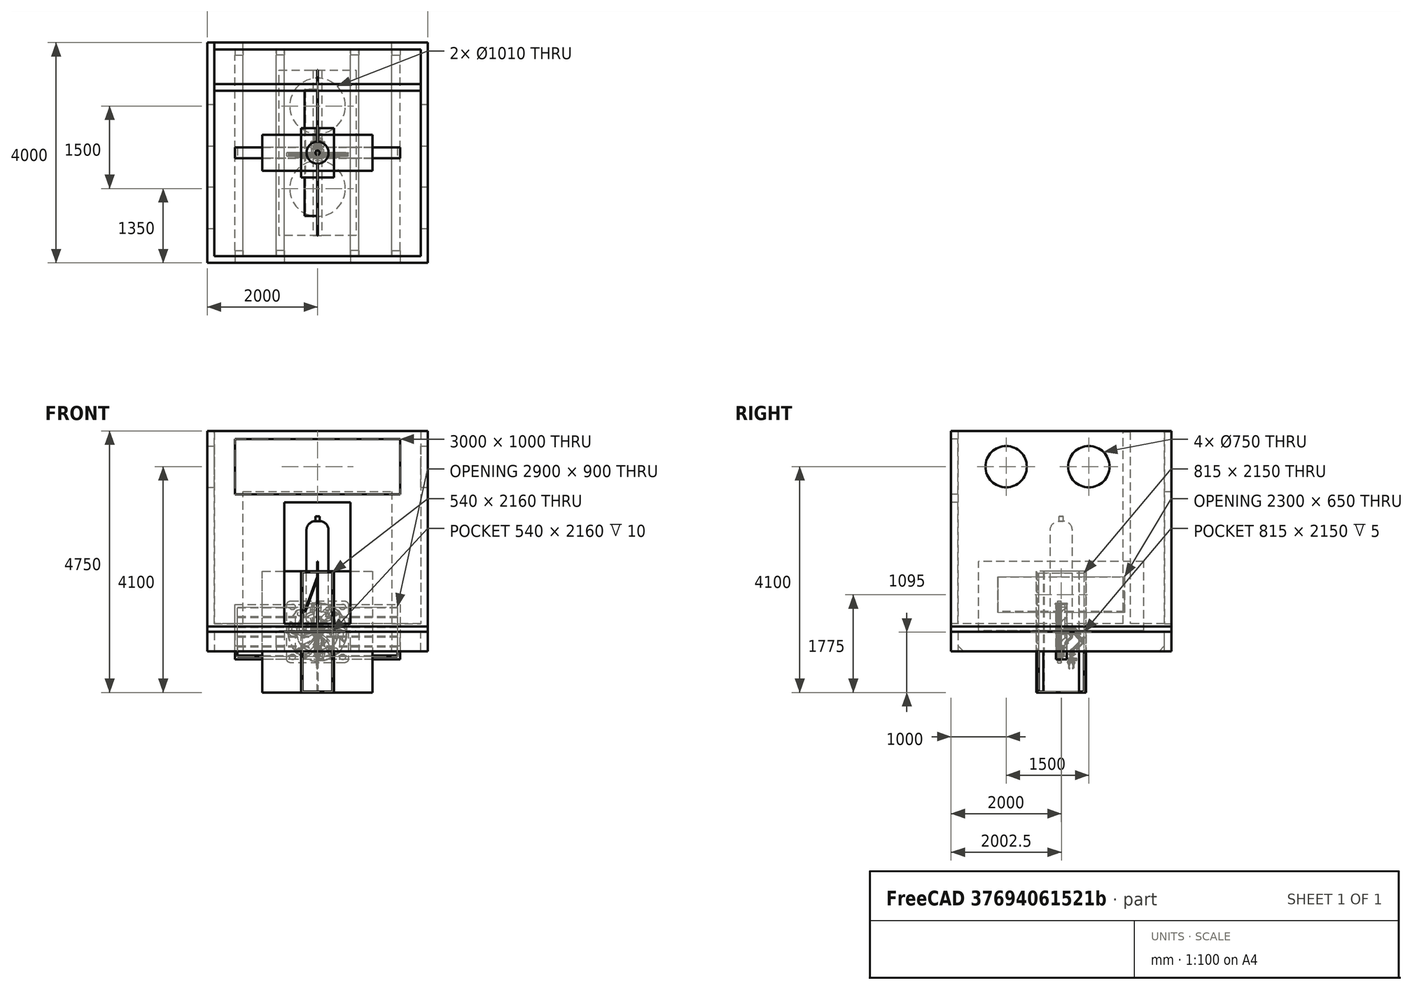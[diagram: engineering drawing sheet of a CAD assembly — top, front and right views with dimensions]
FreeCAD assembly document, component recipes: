
FREECAD ASSEMBLY — COMPONENT RECIPES ("OCPMDC4_v2_asm")

This assembly document has 12 components, labeled P0..P11 below (a component is one placed body or linked part). 9 of them carry a construction recipe — the FreeCAD feature program that regenerates the part from scratch, quoted from this document or its linked companion documents; the rest are supplied as boundary geometry only. No exploded tour is included for this assembly.
COMPONENT P0 — recipe-attached ("AirBox", modeled in this document).
Construction recipe (the document's own serialized feature program — sketch geometry with constraints, then the solid features built on it; lengths are millimeters unless a unit is written):

FEATURE [Sketcher::SketchObject] Sketch018
  MapMode = 5
  Placement = pos=(0,0,0) rot=(1,0,0;1.5708rad)
  Support = -> [XZ_Plane014]
  sketch-geometry (8):
    g0: LineSegment StartX=-1500 StartY=500 StartZ=0 EndX=1500 EndY=500 EndZ=0
    g1: LineSegment StartX=1500 StartY=500 StartZ=0 EndX=1500 EndY=-500 EndZ=0
    g2: LineSegment StartX=1500 StartY=-500 StartZ=0 EndX=-1500 EndY=-500 EndZ=0
    g3: LineSegment StartX=-1500 StartY=-500 StartZ=0 EndX=-1500 EndY=500 EndZ=0
    g4: LineSegment StartX=-1450 StartY=450 StartZ=0 EndX=1450 EndY=450 EndZ=0
    g5: LineSegment StartX=1450 StartY=450 StartZ=0 EndX=1450 EndY=-450 EndZ=0
    g6: LineSegment StartX=1450 StartY=-450 StartZ=0 EndX=-1450 EndY=-450 EndZ=0
    g7: LineSegment StartX=-1450 StartY=-450 StartZ=0 EndX=-1450 EndY=450 EndZ=0
  constraints (21):
    c: Coincident(g0,g1)
    c: Coincident(g1,g2)
    c: Coincident(g2,g3)
    c: Coincident(g3,g0)
    c: Horizontal(g2)
    c: Vertical(g3)
    c: Coincident(g4,g5)
    c: Coincident(g5,g6)
    c: Coincident(g6,g7)
    c: Coincident(g7,g4)
    c: Horizontal(g4)
    c: Horizontal(g6)
    c: Vertical(g7)
    c: Symmetric(g0,g0,g-2)
    c: Symmetric(g0,g1,g-1)
    c: DistanceX(g0,g0) = 3000
    c: DistanceY(g1,g1) = 1000
    c: DistanceX(g4,g0) = 50
    c: DistanceY(g4,g0) = 50
    c: Symmetric(g5,g4,g-1)
    c: DistanceX(g0,g4) = 50
FEATURE [PartDesign::Pad] Pad010
  Direction = (1,1,1)
  Length = 200
  Length2 = 100
  Midplane = true
  Placement = pos=(0,0,0) rot=(1,0,0;1.5708rad)
  Profile = -> Sketch018
  Type = 0
FEATURE [Sketcher::SketchObject] Sketch017
  ExternalGeometry = -> [Pad010]
  MapMode = 5
  Placement = pos=(-1450,0,0) rot=(0.707107,0,0.707107;3.14159rad)
  Support = -> [Pad010]
  sketch-geometry (20):
    g0: LineSegment StartX=450 StartY=-100 StartZ=0 EndX=282.18 EndY=100 EndZ=0
    g1: LineSegment StartX=282.18 StartY=100 StartZ=0 EndX=272.18 EndY=100 EndZ=0
    g2: LineSegment StartX=272.18 StartY=100 StartZ=0 EndX=440 EndY=-100 EndZ=0
    g3: LineSegment StartX=440 StartY=-100 StartZ=0 EndX=450 EndY=-100 EndZ=0
    g4: LineSegment StartX=272.18 StartY=-100 StartZ=0 EndX=104.36 EndY=100 EndZ=0
    g5: LineSegment StartX=104.36 StartY=100 StartZ=0 EndX=94.3601 EndY=100 EndZ=0
    g6: LineSegment StartX=94.3601 StartY=100 StartZ=0 EndX=262.18 EndY=-100 EndZ=0
    g7: LineSegment StartX=262.18 StartY=-100 StartZ=0 EndX=272.18 EndY=-100 EndZ=0
    g8: LineSegment StartX=94.3601 StartY=-100 StartZ=0 EndX=-73.4598 EndY=100 EndZ=0
    g9: LineSegment StartX=-73.4598 StartY=100 StartZ=0 EndX=-83.4598 EndY=100 EndZ=0
    g10: LineSegment StartX=-83.4598 StartY=100 StartZ=0 EndX=84.3601 EndY=-100 EndZ=0
    g11: LineSegment StartX=84.3601 StartY=-100 StartZ=0 EndX=94.3601 EndY=-100 EndZ=0
    g12: LineSegment StartX=-83.4598 StartY=-100 StartZ=0 EndX=-251.28 EndY=100 EndZ=0
    g13: LineSegment StartX=-251.28 StartY=100 StartZ=0 EndX=-261.28 EndY=100 EndZ=0
    g14: LineSegment StartX=-261.28 StartY=100 StartZ=0 EndX=-93.4598 EndY=-100 EndZ=0
    g15: LineSegment StartX=-93.4598 StartY=-100 StartZ=0 EndX=-83.4598 EndY=-100 EndZ=0
    g16: LineSegment StartX=-261.28 StartY=-100 StartZ=0 EndX=-429.1 EndY=100 EndZ=0
    g17: LineSegment StartX=-429.1 StartY=100 StartZ=0 EndX=-439.1 EndY=100 EndZ=0
    g18: LineSegment StartX=-439.1 StartY=100 StartZ=0 EndX=-271.28 EndY=-100 EndZ=0
    g19: LineSegment StartX=-271.28 StartY=-100 StartZ=0 EndX=-261.28 EndY=-100 EndZ=0
  constraints (59):
    c: Coincident(g-6,g0)
    c: PointOnObject(g0,g-5)
    c: Coincident(g0,g1)
    c: Coincident(g1,g2)
    c: PointOnObject(g2,g-6)
    c: Coincident(g2,g3)
    c: Coincident(g3,g0)
    c: PointOnObject(g1,g-5)
    c: Parallel(g2,g0)
    c: DistanceX(g1,g1) = 10
    c: PointOnObject(g4,g-6)
    c: PointOnObject(g4,g-5)
    c: Coincident(g4,g5)
    c: PointOnObject(g5,g-5)
    c: Coincident(g5,g6)
    c: PointOnObject(g6,g-6)
    c: Coincident(g6,g7)
    c: PointOnObject(g8,g-6)
    c: PointOnObject(g8,g-5)
    c: Coincident(g8,g9)
    c: PointOnObject(g9,g-5)
    c: Coincident(g9,g10)
    c: PointOnObject(g10,g-6)
    c: Coincident(g10,g11)
    c: PointOnObject(g12,g-6)
    c: PointOnObject(g12,g-5)
    c: Coincident(g12,g13)
    c: PointOnObject(g13,g-5)
    c: Coincident(g13,g14)
    c: Coincident(g14,g15)
    c: Coincident(g15,g12)
    c: Horizontal(g15)
    c: PointOnObject(g16,g-6)
    c: PointOnObject(g16,g-5)
    c: Coincident(g16,g17)
    c: PointOnObject(g17,g-5)
    c: Coincident(g17,g18)
    c: PointOnObject(g18,g-6)
    c: Coincident(g18,g19)
    c: Coincident(g19,g16)
    c: Angle(g2,g-6) = 0.872665
    c: Coincident(g7,g4)
    c: DistanceX(g5,g5) = 10
    c: Parallel(g6,g4)
    c: Angle(g6,g-6) = 0.872665
    c: Vertical(g4,g1)
    c: DistanceX(g9,g9) = 10
    c: Parallel(g10,g8)
    c: Angle(g10,g-6) = 0.872665
    c: Parallel(g14,g12)
    c: Vertical(g11,g5)
    c: Coincident(g8,g11)
    c: DistanceX(g13,g13) = 10
    c: Vertical(g12,g9)
    c: Angle(g-6,g14) = 2.26893
    c: Parallel(g18,g16)
    c: DistanceX(g17,g17) = 10
    c: Vertical(g16,g13)
    c: Angle(g-6,g18) = 2.26893
FEATURE [PartDesign::Pad] Pad011
  BaseFeature = -> Pad010
  Direction = (1,1,1)
  Length = 2900
  Length2 = 100
  Placement = pos=(0,0,0) rot=(1,0,0;1.5708rad)
  Profile = -> Sketch017
  Type = 0
FEATURE [PartDesign::Body] Body005
  Group = -> [Sketch018,Pad010,Sketch017,Pad011]
  Origin = -> Origin014
  Tip = -> Pad011
COMPONENT P1 — geometry summary ("Fan1000mm"; no construction recipe available for this part):
  bounding box: 1120.0 x 1120.0 x 64.0 mm
  tessellated surface: 43,382 triangles
  volume: 25228396 mm^3 (31% of its bounding box)
COMPONENT P2 — geometry summary ("Fan750mm"; no construction recipe available for this part):
  bounding box: 800.0 x 800.0 x 80.0 mm
  tessellated surface: 39,798 triangles
  volume: 16089539 mm^3 (31% of its bounding box)
COMPONENT P3 — recipe-attached ("HotColdSeperator", modeled in this document).
Construction recipe (the document's own serialized feature program — sketch geometry with constraints, then the solid features built on it; lengths are millimeters unless a unit is written):

FEATURE [Sketcher::SketchObject] Sketch024
  MapMode = 5
  Placement = pos=(0,0,0) rot=(1,0,0;1.5708rad)
  Support = -> [XZ_Plane025]
  sketch-geometry (8):
    g0: LineSegment StartX=-80 StartY=0 StartZ=0 EndX=80 EndY=0 EndZ=0
    g1: LineSegment StartX=80 StartY=0 StartZ=0 EndX=80 EndY=15 EndZ=0
    g2: LineSegment StartX=-80 StartY=15 StartZ=0 EndX=-80 EndY=0 EndZ=0
    g3: LineSegment StartX=-7.5 StartY=15 StartZ=0 EndX=-7.5 EndY=1280 EndZ=0
    g4: LineSegment StartX=-7.5 StartY=1280 StartZ=0 EndX=7.5 EndY=1280 EndZ=0
    g5: LineSegment StartX=7.5 StartY=1280 StartZ=0 EndX=7.5 EndY=15 EndZ=0
    g6: LineSegment StartX=-80 StartY=15 StartZ=0 EndX=-7.5 EndY=15 EndZ=0
    g7: LineSegment StartX=7.5 StartY=15 StartZ=0 EndX=80 EndY=15 EndZ=0
  constraints (22):
    c: Coincident(g0,g1)
    c: Coincident(g2,g0)
    c: Vertical(g1)
    c: Vertical(g2)
    c: PointOnObject(g0,g-1)
    c: Coincident(g3,g4)
    c: Coincident(g4,g5)
    c: Horizontal(g4)
    c: Vertical(g3)
    c: Vertical(g5)
    c: Symmetric(g5,g3,g-2)
    c: DistanceY(g1,g1) = 15
    c: Coincident(g6,g2)
    c: Coincident(g6,g3)
    c: Horizontal(g6)
    c: Coincident(g7,g5)
    c: Coincident(g7,g1)
    c: Horizontal(g7)
    c: Symmetric(g0,g0,g-2)
    c: DistanceX(g3,g5) = 15
    c: DistanceX(g0,g0) = 160
    c: DistanceY(g-1,g4) = 1280
FEATURE [PartDesign::Pad] Pad014
  Direction = (1,1,1)
  Length = 3000
  Length2 = 100
  Midplane = true
  Placement = pos=(0,0,0) rot=(1,0,0;1.5708rad)
  Profile = -> Sketch024
  Type = 0
FEATURE [Sketcher::SketchObject] Sketch022
  ExternalGeometry = -> [Pad014]
  MapMode = 5
  Placement = pos=(7.5,0,0) rot=(0.707107,0,0.707107;3.14159rad)
  Support = -> [Pad014]
  sketch-geometry (4):
    g0: LineSegment StartX=350 StartY=-1150 StartZ=0 EndX=1000 EndY=-1150 EndZ=0
    g1: LineSegment StartX=1000 StartY=-1150 StartZ=0 EndX=1000 EndY=1150 EndZ=0
    g2: LineSegment StartX=1000 StartY=1150 StartZ=0 EndX=350 EndY=1150 EndZ=0
    g3: LineSegment StartX=350 StartY=1150 StartZ=0 EndX=350 EndY=-1150 EndZ=0
  constraints (12):
    c: Coincident(g0,g1)
    c: Coincident(g1,g2)
    c: Coincident(g2,g3)
    c: Coincident(g3,g0)
    c: Horizontal(g0)
    c: Horizontal(g2)
    c: Vertical(g1)
    c: Vertical(g3)
    c: DistanceX(g-3,g2) = 350
    c: DistanceY(g-4,g0) = 350
    c: DistanceY(g2,g-3) = 350
    c: DistanceX(g2,g2) = 650
FEATURE [PartDesign::Pocket] Pocket005
  BaseFeature = -> Pad014
  Length = 5
  Length2 = 100
  Placement = pos=(0,0,0) rot=(1,0,0;1.5708rad)
  Profile = -> Sketch022
  Type = 1
FEATURE [Sketcher::SketchObject] Sketch023
  ExternalGeometry = -> [Pocket005]
  MapMode = 5
  Placement = pos=(0,1150,-2.53e-13) rot=(1,0,0;1.5708rad)
  Support = -> [Pocket005]
  sketch-geometry (4):
    g0: LineSegment StartX=-7.5 StartY=1000 StartZ=0 EndX=7.5 EndY=1000 EndZ=0
    g1: LineSegment StartX=7.5 StartY=1000 StartZ=0 EndX=-218.819 EndY=365.437 EndZ=0
    g2: LineSegment StartX=-218.819 StartY=365.437 StartZ=0 EndX=-231.597 EndY=371.667 EndZ=0
    g3: LineSegment StartX=-231.597 StartY=371.667 StartZ=0 EndX=-7.5 EndY=1000 EndZ=0
  constraints (8):
    c: Coincident(g-4,g0)
    c: Coincident(g0,g-3)
    c: Coincident(g0,g1)
    c: Coincident(g1,g2)
    c: Coincident(g2,g3)
    c: Coincident(g3,g0)
    c: Parallel(g3,g1)
    c: Distance(g3) = 667.1
FEATURE [PartDesign::Pad] Pad015
  BaseFeature = -> Pocket005
  Direction = (1,1,1)
  Length = 2300
  Length2 = 100
  Placement = pos=(0,0,0) rot=(1,0,0;1.5708rad)
  Profile = -> Sketch023
  Type = 0
FEATURE [PartDesign::Body] Body008
  Group = -> [Sketch024,Pad014,Sketch022,Pocket005,Sketch023,Pad015]
  Origin = -> Origin025
  Tip = -> Pad015
COMPONENT P4 — recipe-attached ("Loeschflasche", modeled in this document).
Construction recipe (the document's own serialized feature program — sketch geometry with constraints, then the solid features built on it; lengths are millimeters unless a unit is written):

FEATURE [Sketcher::SketchObject] Sketch014
  MapMode = 5
  Placement = pos=(0,0,0) rot=(1,0,0;1.5708rad)
  Support = -> [XZ_Plane011]
  sketch-geometry (6):
    g0: LineSegment StartX=200 StartY=0 StartZ=0 EndX=200 EndY=1850 EndZ=0
    g1: LineSegment StartX=40 StartY=2010 StartZ=0 EndX=40 EndY=2100 EndZ=0
    g2: LineSegment StartX=200 StartY=0 StartZ=0 EndX=0 EndY=0 EndZ=0
    g3: LineSegment StartX=40 StartY=2100 StartZ=0 EndX=0 EndY=2100 EndZ=0
    g4: LineSegment StartX=0 StartY=2100 StartZ=0 EndX=0 EndY=0 EndZ=0
    g5: ArcOfCircle CenterX=40 CenterY=1850 CenterZ=0 NormalX=0 NormalY=0 NormalZ=1 AngleXU=0 Radius=160 StartAngle=0 EndAngle=1.5708
  constraints (17):
    c: Vertical(g0)
    c: Vertical(g1)
    c: Horizontal(g2)
    c: Vertical(g4)
    c: Coincident(g5,g1)
    c: Horizontal(g3)
    c: Coincident(g3,g1)
    c: Tangent(g5,g0) = -1.5708
    c: Coincident(g0,g2)
    c: Coincident(g2,g4)
    c: Coincident(g2,g-1)
    c: DistanceX(g2,g2) = 200
    c: Perpendicular(g5,g1)
    c: Coincident(g4,g3)
    c: DistanceY(g2,g3) = 2100
    c: DistanceY(g1,g1) = 90
    c: DistanceX(g3,g1) = 40
FEATURE [PartDesign::Revolution] Revolution
  Angle = 360
  Axis = (0,2e-16,1)
  Base = (0,0,0)
  Placement = pos=(0,0,0) rot=(1,0,0;1.5708rad)
  Profile = -> Sketch014
  ReferenceAxis = -> Sketch014 [V_Axis]
  Reversed = true
FEATURE [PartDesign::Body] Body003
  Group = -> [Sketch014,Revolution]
  Origin = -> Origin011
  Tip = -> Revolution
COMPONENT P5 — recipe-attached ("NSV", modeled in this document).
Construction recipe (the document's own serialized feature program — sketch geometry with constraints, then the solid features built on it; lengths are millimeters unless a unit is written):

FEATURE [Sketcher::SketchObject] Sketch016
  MapMode = 5
  Placement = pos=(0,0,0) rot=(1,0,0;1.5708rad)
  Support = -> [XZ_Plane012]
  sketch-geometry (4):
    g0: LineSegment StartX=-1000 StartY=1100 StartZ=0 EndX=1000 EndY=1100 EndZ=0
    g1: LineSegment StartX=1000 StartY=1100 StartZ=0 EndX=1000 EndY=-1100 EndZ=0
    g2: LineSegment StartX=1000 StartY=-1100 StartZ=0 EndX=-1000 EndY=-1100 EndZ=0
    g3: LineSegment StartX=-1000 StartY=-1100 StartZ=0 EndX=-1000 EndY=1100 EndZ=0
  constraints (12):
    c: Coincident(g0,g1)
    c: Coincident(g1,g2)
    c: Coincident(g2,g3)
    c: Coincident(g3,g0)
    c: Horizontal(g0)
    c: Horizontal(g2)
    c: Vertical(g1)
    c: Vertical(g3)
    c: DistanceX(g0,g0) = 2000
    c: DistanceY(g1,g1) = 2200
    c: DistanceY(g-1,g0) = 1100
    c: DistanceX(g-1,g1) = 1000
FEATURE [PartDesign::Pad] Pad009
  Direction = (1,1,1)
  Length = 650
  Length2 = 100
  Midplane = true
  Placement = pos=(0,0,0) rot=(1,0,0;1.5708rad)
  Profile = -> Sketch016
  Type = 0
FEATURE [Sketcher::SketchObject] Sketch015
  ExternalGeometry = -> [Pad009]
  MapMode = 5
  Placement = pos=(0,-325,7.15e-14) rot=(1,0,0;1.5708rad)
  Support = -> [Pad009]
  sketch-geometry (4):
    g0: LineSegment StartX=-5 StartY=1100 StartZ=0 EndX=5 EndY=1100 EndZ=0
    g1: LineSegment StartX=5 StartY=1100 StartZ=0 EndX=5 EndY=-1100 EndZ=0
    g2: LineSegment StartX=5 StartY=-1100 StartZ=0 EndX=-5 EndY=-1100 EndZ=0
    g3: LineSegment StartX=-5 StartY=-1100 StartZ=0 EndX=-5 EndY=1100 EndZ=0
  constraints (11):
    c: Coincident(g0,g1)
    c: Coincident(g1,g2)
    c: Coincident(g2,g3)
    c: Coincident(g3,g0)
    c: Horizontal(g2)
    c: Vertical(g1)
    c: Vertical(g3)
    c: Horizontal(g0,g-3)
    c: DistanceX(g0,g0) = 10
    c: Symmetric(g0,g0,g-2)
    c: Horizontal(g1,g-4)
FEATURE [PartDesign::Pocket] Pocket004
  BaseFeature = -> Pad009
  Length = 10
  Length2 = 100
  Placement = pos=(0,0,0) rot=(1,0,0;1.5708rad)
  Profile = -> Sketch015
  Type = 0
FEATURE [PartDesign::Body] Body004
  Group = -> [Sketch016,Pad009,Sketch015,Pocket004]
  Origin = -> Origin012
  Tip = -> Pocket004
COMPONENT P6 — recipe-attached ("OCPMDC4mv2", modeled in this document).
Construction recipe (the document's own serialized feature program — sketch geometry with constraints, then the solid features built on it; lengths are millimeters unless a unit is written):

FEATURE [Sketcher::SketchObject] Sketch
  MapMode = 5
  Support = -> [XY_Plane]
  sketch-geometry (4):
    g0: LineSegment StartX=-1875 StartY=1875 StartZ=0 EndX=1875 EndY=1875 EndZ=0
    g1: LineSegment StartX=1875 StartY=1875 StartZ=0 EndX=1875 EndY=-1875 EndZ=0
    g2: LineSegment StartX=1875 StartY=-1875 StartZ=0 EndX=-1875 EndY=-1875 EndZ=0
    g3: LineSegment StartX=-1875 StartY=-1875 StartZ=0 EndX=-1875 EndY=1875 EndZ=0
  constraints (10):
    c: Coincident(g0,g1)
    c: Coincident(g1,g2)
    c: Coincident(g2,g3)
    c: Coincident(g3,g0)
    c: Horizontal(g2)
    c: Vertical(g3)
    c: DistanceX(g0,g0) = 3750
    c: DistanceY(g1,g1) = 3750
    c: Symmetric(g0,g0,g-2)
    c: Symmetric(g0,g1,g-1)
FEATURE [PartDesign::Pad] Pad
  Direction = (1,1,1)
  Length = 150
  Length2 = 100
  Profile = -> Sketch
  Type = 0
FEATURE [Sketcher::SketchObject] Sketch001
  ExternalGeometry = -> [Pad]
  MapMode = 5
  Placement = pos=(0,-1875,0) rot=(1,0,0;1.5708rad)
  Support = -> [Pad]
  sketch-geometry (16):
    g0: LineSegment StartX=-1350 StartY=0 StartZ=0 EndX=-1500 EndY=0 EndZ=0
    g1: LineSegment StartX=-1500 StartY=0 StartZ=0 EndX=-1500 EndY=-350 EndZ=0
    g2: LineSegment StartX=-1500 StartY=-350 StartZ=0 EndX=-1350 EndY=-350 EndZ=0
    g3: LineSegment StartX=-1350 StartY=-350 StartZ=0 EndX=-1350 EndY=0 EndZ=0
    g4: LineSegment StartX=-750 StartY=0 StartZ=0 EndX=-600 EndY=0 EndZ=0
    g5: LineSegment StartX=-600 StartY=0 StartZ=0 EndX=-600 EndY=-350 EndZ=0
    g6: LineSegment StartX=-600 StartY=-350 StartZ=0 EndX=-750 EndY=-350 EndZ=0
    g7: LineSegment StartX=-750 StartY=-350 StartZ=0 EndX=-750 EndY=0 EndZ=0
    g8: LineSegment StartX=600 StartY=0 StartZ=0 EndX=750 EndY=0 EndZ=0
    g9: LineSegment StartX=750 StartY=0 StartZ=0 EndX=750 EndY=-350 EndZ=0
    g10: LineSegment StartX=750 StartY=-350 StartZ=0 EndX=600 EndY=-350 EndZ=0
    g11: LineSegment StartX=600 StartY=-350 StartZ=0 EndX=600 EndY=0 EndZ=0
    g12: LineSegment StartX=1500 StartY=0 StartZ=0 EndX=1350 EndY=0 EndZ=0
    g13: LineSegment StartX=1350 StartY=0 StartZ=0 EndX=1350 EndY=-350 EndZ=0
    g14: LineSegment StartX=1350 StartY=-350 StartZ=0 EndX=1500 EndY=-350 EndZ=0
    g15: LineSegment StartX=1500 StartY=-350 StartZ=0 EndX=1500 EndY=0 EndZ=0
  constraints (48):
    c: Coincident(g0,g1)
    c: Coincident(g1,g2)
    c: Coincident(g2,g3)
    c: Coincident(g3,g0)
    c: Horizontal(g0)
    c: Horizontal(g2)
    c: Vertical(g1)
    c: Vertical(g3)
    c: PointOnObject(g0,g-1)
    c: DistanceX(g0,g0) = 150
    c: DistanceY(g2,g-1) = 350
    c: Coincident(g4,g5)
    c: Coincident(g5,g6)
    c: Coincident(g6,g7)
    c: Coincident(g7,g4)
    c: Horizontal(g4)
    c: Horizontal(g6)
    c: Vertical(g5)
    c: Vertical(g7)
    c: PointOnObject(g4,g-1)
    c: Coincident(g8,g9)
    c: Coincident(g9,g10)
    c: Coincident(g10,g11)
    c: Coincident(g11,g8)
    c: Horizontal(g8)
    c: Horizontal(g10)
    c: Vertical(g9)
    c: Vertical(g11)
    c: PointOnObject(g8,g-1)
    c: Coincident(g12,g13)
    c: Coincident(g13,g14)
    c: Coincident(g14,g15)
    c: Coincident(g15,g12)
    c: Horizontal(g12)
    c: Horizontal(g14)
    c: Vertical(g13)
    c: Vertical(g15)
    c: PointOnObject(g12,g-1)
    c: Horizontal(g6,g1)
    c: Horizontal(g1,g10)
    c: Horizontal(g10,g13)
    c: DistanceX(g4,g4) = 150
    c: DistanceX(g-3,g4) = 1275
    c: DistanceX(g-3,g0) = 375
    c: DistanceX(g12,g-4) = 375
    c: DistanceX(g12,g12) = 150
    c: DistanceX(g8,g-4) = 1275
    c: DistanceX(g8,g8) = 150
FEATURE [PartDesign::Pad] Pad001
  BaseFeature = -> Pad
  Direction = (1,1,1)
  Length = 3750
  Length2 = 100
  Profile = -> Sketch001
  Reversed = true
  Type = 0
FEATURE [PartDesign::Chamfer] Chamfer
  Angle = 45
  Base = -> Pad001 [Edge52,Edge58,Edge63,Edge67,Edge40,Edge34,Edge28,Edge22]
  BaseFeature = -> Pad001
  ChamferType = 0
  FlipDirection = false
  Size = 100
  Size2 = 1
  SupportTransform = false
FEATURE [Sketcher::SketchObject] Sketch002
  ExternalGeometry = -> [Chamfer]
  MapMode = 5
  Placement = pos=(-1875,0,0) rot=(0.57735,-0.57735,-0.57735;2.0944rad)
  Support = -> [Chamfer]
  sketch-geometry (4):
    g0: LineSegment StartX=-2000 StartY=-350 StartZ=0 EndX=2000 EndY=-350 EndZ=0
    g1: LineSegment StartX=2000 StartY=-350 StartZ=0 EndX=2000 EndY=3650 EndZ=0
    g2: LineSegment StartX=2000 StartY=3650 StartZ=0 EndX=-2000 EndY=3650 EndZ=0
    g3: LineSegment StartX=-2000 StartY=3650 StartZ=0 EndX=-2000 EndY=-350 EndZ=0
  constraints (12):
    c: Coincident(g0,g1)
    c: Coincident(g1,g2)
    c: Coincident(g2,g3)
    c: Coincident(g3,g0)
    c: Horizontal(g0)
    c: Horizontal(g2)
    c: Vertical(g1)
    c: Vertical(g3)
    c: DistanceX(g2,g2) = 4000
    c: DistanceY(g1,g1) = 4000
    c: DistanceX(g-1,g0) = 2000
    c: Horizontal(g0,g-5)
FEATURE [PartDesign::Pad] Pad002
  BaseFeature = -> Chamfer
  Direction = (1,1,1)
  Length = 125
  Length2 = 100
  Profile = -> Sketch002
  Type = 0
FEATURE [Sketcher::SketchObject] Sketch003
  ExternalGeometry = -> [Pad002]
  MapMode = 5
  Placement = pos=(1875,0,0) rot=(0.57735,0.57735,0.57735;2.0944rad)
  Support = -> [Pad002]
  sketch-geometry (4):
    g0: LineSegment StartX=1250 StartY=150 StartZ=0 EndX=1125 EndY=150 EndZ=0
    g1: LineSegment StartX=1125 StartY=150 StartZ=0 EndX=1125 EndY=3637.44 EndZ=0
    g2: LineSegment StartX=1125 StartY=3637.44 StartZ=0 EndX=1250 EndY=3637.44 EndZ=0
    g3: LineSegment StartX=1250 StartY=3637.44 StartZ=0 EndX=1250 EndY=150 EndZ=0
  constraints (12):
    c: Coincident(g0,g1)
    c: Coincident(g1,g2)
    c: Coincident(g2,g3)
    c: Coincident(g3,g0)
    c: Horizontal(g0)
    c: Horizontal(g2)
    c: Vertical(g1)
    c: Vertical(g3)
    c: PointOnObject(g0,g-7)
    c: DistanceX(g2,g2) = 125
    c: DistanceX(g-7,g1) = 3000
    c: DistanceY(g3,g3) = 3487.44
FEATURE [PartDesign::Pad] Pad003
  BaseFeature = -> Pad002
  Direction = (1,1,1)
  Length = 3750
  Length2 = 100
  Profile = -> Sketch003
  Reversed = true
  Type = 0
FEATURE [Sketcher::SketchObject] Sketch004
  ExternalGeometry = -> [Pad003]
  MapMode = 5
  Placement = pos=(1875,0,0) rot=(0.57735,0.57735,0.57735;2.0944rad)
  Support = -> [Pad003]
  sketch-geometry (4):
    g0: LineSegment StartX=-2000 StartY=3650 StartZ=0 EndX=2000 EndY=3650 EndZ=0
    g1: LineSegment StartX=2000 StartY=3650 StartZ=0 EndX=2000 EndY=-350 EndZ=0
    g2: LineSegment StartX=2000 StartY=-350 StartZ=0 EndX=-2000 EndY=-350 EndZ=0
    g3: LineSegment StartX=-2000 StartY=-350 StartZ=0 EndX=-2000 EndY=3650 EndZ=0
  constraints (10):
    c: Coincident(g0,g1)
    c: Coincident(g1,g2)
    c: Coincident(g2,g3)
    c: Coincident(g3,g0)
    c: Horizontal(g0)
    c: Horizontal(g2)
    c: Vertical(g1)
    c: Vertical(g3)
    c: Coincident(g0,g-4)
    c: Coincident(g1,g-5)
FEATURE [PartDesign::Pad] Pad004
  BaseFeature = -> Pad003
  Direction = (1,1,1)
  Length = 125
  Length2 = 100
  Profile = -> Sketch004
  Type = 0
FEATURE [Sketcher::SketchObject] Sketch005
  ExternalGeometry = -> [Pad004]
  MapMode = 5
  Placement = pos=(0,-1875,0) rot=(1,0,0;1.5708rad)
  Support = -> [Pad004]
  sketch-geometry (12):
    g0: LineSegment StartX=-1875 StartY=3650 StartZ=0 EndX=1875 EndY=3650 EndZ=0
    g1: LineSegment StartX=1875 StartY=3650 StartZ=0 EndX=1875 EndY=-350 EndZ=0
    g2: LineSegment StartX=1875 StartY=-350 StartZ=0 EndX=-1875 EndY=-350 EndZ=0
    g3: LineSegment StartX=-1875 StartY=-350 StartZ=0 EndX=-1875 EndY=3650 EndZ=0
    g4: LineSegment StartX=-600 StartY=150 StartZ=0 EndX=600 EndY=150 EndZ=0
    g5: LineSegment StartX=600 StartY=150 StartZ=0 EndX=600 EndY=2350 EndZ=0
    g6: LineSegment StartX=600 StartY=2350 StartZ=0 EndX=-600 EndY=2350 EndZ=0
    g7: LineSegment StartX=-600 StartY=2350 StartZ=0 EndX=-600 EndY=150 EndZ=0
    g8: LineSegment StartX=-1500 StartY=3500 StartZ=0 EndX=1500 EndY=3500 EndZ=0
    g9: LineSegment StartX=1500 StartY=3500 StartZ=0 EndX=1500 EndY=2500 EndZ=0
    g10: LineSegment StartX=1500 StartY=2500 StartZ=0 EndX=-1500 EndY=2500 EndZ=0
    g11: LineSegment StartX=-1500 StartY=2500 StartZ=0 EndX=-1500 EndY=3500 EndZ=0
  constraints (33):
    c: Coincident(g0,g1)
    c: Coincident(g1,g2)
    c: Coincident(g2,g3)
    c: Coincident(g3,g0)
    c: Horizontal(g0)
    c: Horizontal(g2)
    c: Vertical(g1)
    c: Vertical(g3)
    c: Coincident(g0,g-4)
    c: Coincident(g1,g-6)
    c: Coincident(g4,g5)
    c: Coincident(g5,g6)
    c: Coincident(g6,g7)
    c: Coincident(g7,g4)
    c: Horizontal(g4)
    c: Horizontal(g6)
    c: Vertical(g5)
    c: Vertical(g7)
    c: PointOnObject(g4,g-7)
    c: DistanceX(g6,g6) = 1200
    c: DistanceY(g-1,g5) = 2350
    c: DistanceX(g-1,g4) = 600
    c: Coincident(g8,g9)
    c: Coincident(g9,g10)
    c: Coincident(g10,g11)
    c: Coincident(g11,g8)
    c: Horizontal(g10)
    c: Vertical(g9)
    c: Vertical(g11)
    c: Symmetric(g8,g8,g-2)
    c: DistanceY(g-1,g9) = 2500
    c: DistanceY(g9,g9) = 1000
    c: DistanceX(g8,g8) = 3000
FEATURE [PartDesign::Pad] Pad005
  BaseFeature = -> Pad004
  Direction = (1,1,1)
  Length = 125
  Length2 = 100
  Profile = -> Sketch005
  Type = 0
FEATURE [Sketcher::SketchObject] Sketch006
  ExternalGeometry = -> [Pad005]
  MapMode = 5
  Placement = pos=(0,1875,0) rot=(0,0.707107,0.707107;3.14159rad)
  Support = -> [Pad005]
  sketch-geometry (8):
    g0: LineSegment StartX=-1875 StartY=3650 StartZ=0 EndX=1875 EndY=3637.44 EndZ=0
    g1: LineSegment StartX=1875 StartY=-350 StartZ=0 EndX=-1875 EndY=-350 EndZ=0
    g2: LineSegment StartX=-1875 StartY=-350 StartZ=0 EndX=-1875 EndY=3650 EndZ=0
    g3: LineSegment StartX=-1350 StartY=150 StartZ=0 EndX=1350 EndY=150 EndZ=0
    g4: LineSegment StartX=1350 StartY=150 StartZ=0 EndX=1350 EndY=2550 EndZ=0
    g5: LineSegment StartX=1350 StartY=2550 StartZ=0 EndX=-1350 EndY=2550 EndZ=0
    g6: LineSegment StartX=-1350 StartY=2550 StartZ=0 EndX=-1350 EndY=150 EndZ=0
    g7: LineSegment StartX=1875 StartY=3637.44 StartZ=0 EndX=1875 EndY=-350 EndZ=0
  constraints (20):
    c: Coincident(g1,g2)
    c: Coincident(g2,g0)
    c: Vertical(g2)
    c: Coincident(g3,g4)
    c: Coincident(g4,g5)
    c: Coincident(g5,g6)
    c: Coincident(g6,g3)
    c: Horizontal(g3)
    c: Horizontal(g5)
    c: Vertical(g4)
    c: Vertical(g6)
    c: PointOnObject(g3,g-5)
    c: DistanceX(g5,g-1) = 1350
    c: DistanceX(g-1,g4) = 1350
    c: DistanceY(g-1,g4) = 2550
    c: Coincident(g-6,g1)
    c: Coincident(g0,g-7)
    c: Coincident(g7,g0)
    c: Coincident(g7,g1)
    c: Coincident(g1,g-4)
FEATURE [PartDesign::Pad] Pad006
  BaseFeature = -> Pad005
  Direction = (1,1,1)
  Length = 125
  Length2 = 100
  Profile = -> Sketch006
  Type = 0
FEATURE [Sketcher::SketchObject] Sketch008
  MapMode = 5
  Placement = pos=(0,1850,-1.054e-12) rot=(0,0.707107,0.707107;3.14159rad)
  sketch-geometry (4):
    g0: LineSegment StartX=385.941 StartY=1661.56 StartZ=0 EndX=683.703 EndY=1661.56 EndZ=0
    g1: LineSegment StartX=683.703 StartY=1661.56 StartZ=0 EndX=683.703 EndY=1503.07 EndZ=0
    g2: LineSegment StartX=683.703 StartY=1503.07 StartZ=0 EndX=385.941 EndY=1503.07 EndZ=0
    g3: LineSegment StartX=385.941 StartY=1503.07 StartZ=0 EndX=385.941 EndY=1661.56 EndZ=0
  constraints (8):
    c: Coincident(g0,g1)
    c: Coincident(g1,g2)
    c: Coincident(g2,g3)
    c: Coincident(g3,g0)
    c: Horizontal(g0)
    c: Horizontal(g2)
    c: Vertical(g1)
    c: Vertical(g3)
FEATURE [PartDesign::Pocket] Pocket
  BaseFeature = -> Pad006
  Length = 5
  Length2 = 100
  Profile = -> Sketch008
  Type = 0
FEATURE [Sketcher::SketchObject] Sketch009
  ExternalGeometry = -> [Pad006]
  MapMode = 5
  Placement = pos=(2000,0,0) rot=(0.57735,0.57735,0.57735;2.0944rad)
  Support = -> [Pad006]
  sketch-geometry (2):
    g0: Circle CenterX=-1000 CenterY=3000 CenterZ=0 NormalX=0 NormalY=0 NormalZ=1 AngleXU=0 Radius=375
    g1: Circle CenterX=500 CenterY=3000 CenterZ=0 NormalX=0 NormalY=0 NormalZ=1 AngleXU=0 Radius=375
  constraints (6):
    c: Horizontal(g1,g0)
    c: Equal(g1,g0)
    c: Radius(g1) = 375
    c: DistanceX(g0,g1) = 1500
    c: DistanceX(g1,g-4) = 1500
    c: DistanceY(g-1,g1) = 3000
FEATURE [PartDesign::Pocket] Pocket001
  BaseFeature = -> Pocket
  Length = 5
  Length2 = 100
  Profile = -> Sketch009
  Type = 1
FEATURE [PartDesign::Body] Body
  Group = -> [Sketch,Pad,Sketch001,Pad001,Chamfer,Sketch002,Pad002,Sketch003,Pad003,Sketch004,Pad004,Sketch005,Pad005,Sketch006,Pad006,Sketch008,Pocket,Sketch009,Pocket001]
  Origin = -> Origin
  Tip = -> Pocket001
COMPONENT P7 — recipe-attached ("OCPceiling", modeled in this document).
Construction recipe (the document's own serialized feature program — sketch geometry with constraints, then the solid features built on it; lengths are millimeters unless a unit is written):

FEATURE [Sketcher::SketchObject] Sketch021
  MapMode = 5
  Support = -> [XY_Plane023]
  sketch-geometry (6):
    g0: LineSegment StartX=-700 StartY=1500 StartZ=0 EndX=700 EndY=1500 EndZ=0
    g1: LineSegment StartX=700 StartY=1500 StartZ=0 EndX=700 EndY=-1500 EndZ=0
    g2: LineSegment StartX=700 StartY=-1500 StartZ=0 EndX=-700 EndY=-1500 EndZ=0
    g3: LineSegment StartX=-700 StartY=-1500 StartZ=0 EndX=-700 EndY=1500 EndZ=0
    g4: Circle CenterX=0 CenterY=850 CenterZ=0 NormalX=0 NormalY=0 NormalZ=1 AngleXU=0 Radius=505
    g5: Circle CenterX=0 CenterY=-650 CenterZ=0 NormalX=0 NormalY=0 NormalZ=1 AngleXU=0 Radius=505
  constraints (16):
    c: Coincident(g0,g1)
    c: Coincident(g1,g2)
    c: Coincident(g2,g3)
    c: Coincident(g3,g0)
    c: Horizontal(g2)
    c: Vertical(g3)
    c: DistanceY(g1,g1) = 3000
    c: DistanceX(g0,g0) = 1400
    c: Symmetric(g0,g0,g-2)
    c: Symmetric(g0,g1,g-1)
    c: PointOnObject(g4,g-2)
    c: PointOnObject(g5,g-2)
    c: Equal(g4,g5)
    c: Radius(g4) = 505
    c: DistanceY(g5,g4) = 1500
    c: DistanceY(g-1,g4) = 850
FEATURE [PartDesign::Pad] Pad013
  Direction = (1,1,1)
  Length = 20
  Length2 = 100
  Profile = -> Sketch021
  Type = 0
FEATURE [PartDesign::Body] Body007
  Group = -> [Sketch021,Pad013]
  Origin = -> Origin023
  Tip = -> Pad013
COMPONENT P8 — recipe-attached ("OCPRack001", modeled in this document).
Construction recipe (the document's own serialized feature program — sketch geometry with constraints, then the solid features built on it; lengths are millimeters unless a unit is written):

FEATURE [Sketcher::SketchObject] Sketch012
  MapMode = 5
  Placement = pos=(0,0,0) rot=(1,0,0;1.5708rad)
  Support = -> [XZ_Plane009]
  sketch-geometry (4):
    g0: LineSegment StartX=-300 StartY=1100 StartZ=0 EndX=300 EndY=1100 EndZ=0
    g1: LineSegment StartX=300 StartY=1100 StartZ=0 EndX=300 EndY=-1100 EndZ=0
    g2: LineSegment StartX=300 StartY=-1100 StartZ=0 EndX=-300 EndY=-1100 EndZ=0
    g3: LineSegment StartX=-300 StartY=-1100 StartZ=0 EndX=-300 EndY=1100 EndZ=0
  constraints (12):
    c: Coincident(g0,g1)
    c: Coincident(g1,g2)
    c: Coincident(g2,g3)
    c: Coincident(g3,g0)
    c: Horizontal(g0)
    c: Horizontal(g2)
    c: Vertical(g1)
    c: Vertical(g3)
    c: DistanceX(g-1,g0) = 300
    c: DistanceX(g0,g0) = 600
    c: DistanceY(g1,g1) = 2200
    c: DistanceY(g-1,g0) = 1100
FEATURE [PartDesign::Pad] Pad007
  Direction = (1,1,1)
  Length = 900
  Length2 = 100
  Midplane = true
  Placement = pos=(0,0,0) rot=(1,0,0;1.5708rad)
  Profile = -> Sketch012
  Type = 0
FEATURE [Sketcher::SketchObject] Sketch010
  ExternalGeometry = -> [Pad007]
  MapMode = 5
  Placement = pos=(0,-450,9.9e-14) rot=(1,0,0;1.5708rad)
  Support = -> [Pad007]
  sketch-geometry (4):
    g0: LineSegment StartX=-270 StartY=1080 StartZ=0 EndX=270 EndY=1080 EndZ=0
    g1: LineSegment StartX=270 StartY=1080 StartZ=0 EndX=270 EndY=-1080 EndZ=0
    g2: LineSegment StartX=270 StartY=-1080 StartZ=0 EndX=-270 EndY=-1080 EndZ=0
    g3: LineSegment StartX=-270 StartY=-1080 StartZ=0 EndX=-270 EndY=1080 EndZ=0
  constraints (12):
    c: Coincident(g0,g1)
    c: Coincident(g1,g2)
    c: Coincident(g2,g3)
    c: Coincident(g3,g0)
    c: Horizontal(g0)
    c: Horizontal(g2)
    c: Vertical(g1)
    c: Vertical(g3)
    c: DistanceY(g0,g-3) = 20
    c: DistanceX(g0,g-3) = 30
    c: DistanceY(g-6,g1) = 20
    c: DistanceX(g-5,g2) = 30
FEATURE [PartDesign::Pocket] Pocket002
  BaseFeature = -> Pad007
  Length = 10
  Length2 = 100
  Placement = pos=(0,0,0) rot=(1,0,0;1.5708rad)
  Profile = -> Sketch010
  Type = 0
FEATURE [PartDesign::Mirrored] Mirrored
  BaseFeature = -> Pocket002
  MirrorPlane = -> XZ_Plane009
  Originals = -> [Pocket002]
  Placement = pos=(0,0,0) rot=(1,0,0;1.5708rad)
FEATURE [Sketcher::SketchObject] Sketch011
  ExternalGeometry = -> [Mirrored]
  MapMode = 5
  Placement = pos=(300,0,0) rot=(0.707107,0,0.707107;3.14159rad)
  Support = -> [Mirrored]
  sketch-geometry (4):
    g0: LineSegment StartX=-1080 StartY=405 StartZ=0 EndX=1070 EndY=405 EndZ=0
    g1: LineSegment StartX=1070 StartY=405 StartZ=0 EndX=1070 EndY=-410 EndZ=0
    g2: LineSegment StartX=1070 StartY=-410 StartZ=0 EndX=-1080 EndY=-410 EndZ=0
    g3: LineSegment StartX=-1080 StartY=-410 StartZ=0 EndX=-1080 EndY=405 EndZ=0
  constraints (12):
    c: Coincident(g0,g1)
    c: Coincident(g1,g2)
    c: Coincident(g2,g3)
    c: Coincident(g3,g0)
    c: Horizontal(g0)
    c: Horizontal(g2)
    c: Vertical(g1)
    c: Vertical(g3)
    c: DistanceX(g-4,g2) = 20
    c: DistanceY(g-4,g2) = 40
    c: DistanceX(g0,g-6) = 30
    c: DistanceY(g0,g-6) = 45
FEATURE [PartDesign::Pocket] Pocket003
  BaseFeature = -> Mirrored
  Length = 5
  Length2 = 100
  Placement = pos=(0,0,0) rot=(1,0,0;1.5708rad)
  Profile = -> Sketch011
  Type = 0
FEATURE [PartDesign::Mirrored] Mirrored001
  BaseFeature = -> Pocket003
  MirrorPlane = -> YZ_Plane009
  Originals = -> [Pocket003]
  Placement = pos=(0,0,0) rot=(1,0,0;1.5708rad)
FEATURE [PartDesign::Body] Body001
  Group = -> [Sketch012,Pad007,Sketch010,Pocket002,Mirrored,Sketch011,Pocket003,Mirrored001]
  Origin = -> Origin009
  Tip = -> Mirrored001
COMPONENT P9 — geometry summary ("Robotarm"; no construction recipe available for this part):
  bounding box: 785.5 x 426.9 x 248.2 mm
  tessellated surface: 39,688 triangles
  volume: 2591912 mm^3 (3% of its bounding box)
COMPONENT P10 — recipe-attached ("Roof", modeled in this document).
Construction recipe (the document's own serialized feature program — sketch geometry with constraints, then the solid features built on it; lengths are millimeters unless a unit is written):

FEATURE [Sketcher::SketchObject] Sketch013
  MapMode = 5
  Support = -> [XY_Plane010]
  sketch-geometry (4):
    g0: LineSegment StartX=-2000 StartY=2000 StartZ=0 EndX=2000 EndY=2000 EndZ=0
    g1: LineSegment StartX=2000 StartY=2000 StartZ=0 EndX=2000 EndY=-2000 EndZ=0
    g2: LineSegment StartX=2000 StartY=-2000 StartZ=0 EndX=-2000 EndY=-2000 EndZ=0
    g3: LineSegment StartX=-2000 StartY=-2000 StartZ=0 EndX=-2000 EndY=2000 EndZ=0
  constraints (10):
    c: Coincident(g0,g1)
    c: Coincident(g1,g2)
    c: Coincident(g2,g3)
    c: Coincident(g3,g0)
    c: Horizontal(g2)
    c: Vertical(g3)
    c: DistanceX(g0,g0) = 4000
    c: DistanceY(g3,g3) = 4000
    c: Symmetric(g0,g0,g-2)
    c: Symmetric(g0,g1,g-1)
FEATURE [PartDesign::Pad] Pad008
  Direction = (1,1,1)
  Length = 100
  Length2 = 100
  Profile = -> Sketch013
  Type = 0
FEATURE [PartDesign::Body] Body002
  Group = -> [Sketch013,Pad008]
  Origin = -> Origin010
  Tip = -> Pad008
COMPONENT P11 — recipe-attached ("Schraubenfundament", modeled in this document).
Construction recipe (the document's own serialized feature program — sketch geometry with constraints, then the solid features built on it; lengths are millimeters unless a unit is written):

FEATURE [Sketcher::SketchObject] Sketch019
  MapMode = 5
  Placement = pos=(0,0,0) rot=(1,0,0;1.5708rad)
  Support = -> [XZ_Plane016]
  sketch-geometry (24):
    g0: LineSegment StartX=0 StartY=-500 StartZ=0 EndX=0 EndY=500 EndZ=0
    g1: LineSegment StartX=0 StartY=500 StartZ=0 EndX=60 EndY=500 EndZ=0
    g2: LineSegment StartX=60 StartY=500 StartZ=0 EndX=60 EndY=-250 EndZ=0
    g3: LineSegment StartX=60 StartY=-250 StartZ=0 EndX=30 EndY=-267.321 EndZ=0
    g4: LineSegment StartX=30 StartY=-267.321 StartZ=0 EndX=60 EndY=-267.321 EndZ=0
    g5: LineSegment StartX=60 StartY=-267.321 StartZ=0 EndX=30 EndY=-284.641 EndZ=0
    g6: LineSegment StartX=30 StartY=-284.641 StartZ=0 EndX=60 EndY=-284.641 EndZ=0
    g7: LineSegment StartX=60 StartY=-284.641 StartZ=0 EndX=30 EndY=-301.962 EndZ=0
    g8: LineSegment StartX=30 StartY=-301.962 StartZ=0 EndX=60 EndY=-301.962 EndZ=0
    g9: LineSegment StartX=60 StartY=-301.962 StartZ=0 EndX=30 EndY=-319.282 EndZ=0
    g10: LineSegment StartX=30 StartY=-319.282 StartZ=0 EndX=60 EndY=-319.282 EndZ=0
    g11: LineSegment StartX=60 StartY=-319.282 StartZ=0 EndX=30 EndY=-336.603 EndZ=0
    g12: LineSegment StartX=30 StartY=-336.603 StartZ=0 EndX=60 EndY=-336.603 EndZ=0
    g13: LineSegment StartX=60 StartY=-336.603 StartZ=0 EndX=30 EndY=-353.923 EndZ=0
    g14: LineSegment StartX=30 StartY=-353.923 StartZ=0 EndX=60 EndY=-353.923 EndZ=0
    g15: LineSegment StartX=60 StartY=-353.923 StartZ=0 EndX=30 EndY=-371.244 EndZ=0
    g16: LineSegment StartX=30 StartY=-371.244 StartZ=0 EndX=60 EndY=-371.244 EndZ=0
    g17: LineSegment StartX=60 StartY=-371.244 StartZ=0 EndX=30 EndY=-388.564 EndZ=0
    g18: LineSegment StartX=30 StartY=-388.564 StartZ=0 EndX=60 EndY=-388.564 EndZ=0
    g19: LineSegment StartX=60 StartY=-388.564 StartZ=0 EndX=30 EndY=-405.885 EndZ=0
    g20: LineSegment StartX=30 StartY=-405.885 StartZ=0 EndX=60 EndY=-405.885 EndZ=0
    g21: LineSegment StartX=60 StartY=-405.885 StartZ=0 EndX=30 EndY=-423.205 EndZ=0
    g22: LineSegment StartX=30 StartY=-423.205 StartZ=0 EndX=60 EndY=-423.205 EndZ=0
    g23: LineSegment StartX=60 StartY=-423.205 StartZ=0 EndX=0 EndY=-500 EndZ=0
  constraints (72):
    c: Vertical(g0)
    c: Coincident(g0,g1)
    c: Horizontal(g1)
    c: Coincident(g1,g2)
    c: Vertical(g2)
    c: Coincident(g2,g3)
    c: Coincident(g3,g4)
    c: Coincident(g4,g5)
    c: Coincident(g5,g6)
    c: Coincident(g6,g7)
    c: Coincident(g7,g8)
    c: Horizontal(g8)
    c: Coincident(g8,g9)
    c: Coincident(g9,g10)
    c: Coincident(g10,g11)
    c: Coincident(g11,g12)
    c: Coincident(g12,g13)
    c: Coincident(g13,g14)
    c: Coincident(g14,g15)
    c: Coincident(g15,g16)
    c: Coincident(g16,g17)
    c: Coincident(g17,g18)
    c: Coincident(g18,g19)
    c: Coincident(g19,g20)
    c: Coincident(g20,g21)
    c: Coincident(g21,g22)
    c: Vertical(g4,g6)
    c: Vertical(g6,g8)
    c: Vertical(g8,g10)
    c: Vertical(g10,g12)
    c: Vertical(g12,g14)
    c: Vertical(g14,g16)
    c: Vertical(g16,g18)
    c: Vertical(g18,g20)
    c: Vertical(g20,g22)
    c: Vertical(g3,g5)
    c: Vertical(g5,g7)
    c: Vertical(g7,g9)
    c: Vertical(g9,g11)
    c: Vertical(g11,g13)
    c: Vertical(g13,g15)
    c: Vertical(g15,g17)
    c: Vertical(g17,g19)
    c: Vertical(g19,g21)
    c: Angle(g4,g3) = 0.523599
    c: Angle(g6,g5) = 0.523599
    c: Angle(g4,g5) = 0.523599
    c: Angle(g6,g7) = 0.523599
    c: Angle(g8,g7) = 0.523599
    c: DistanceX(g3,g4) = 30
    c: Angle(g8,g9) = 0.523599
    c: Angle(g10,g9) = 0.523599
    c: Angle(g12,g11) = 0.523599
    c: Angle(g10,g11) = 0.523599
    c: Angle(g12,g13) = 0.523599
    c: Angle(g14,g13) = 0.523599
    c: Angle(g14,g15) = 0.523599
    c: Angle(g16,g15) = 0.523599
    c: Angle(g16,g17) = 0.523599
    c: Angle(g18,g17) = 0.523599
    c: Angle(g18,g19) = 0.523599
    c: Angle(g20,g19) = 0.523599
    c: Angle(g20,g21) = 0.523599
    c: Angle(g22,g21) = 0.523599
    c: DistanceY(g0,g0) = 1000
    c: Coincident(g23,g22)
    c: Coincident(g23,g0)
    c: DistanceY(g-1,g0) = 500
    c: Vertical(g2,g4)
    c: DistanceX(g0,g1) = 60
    c: PointOnObject(g-1,g0)
    c: DistanceY(g2,g1) = 750
FEATURE [PartDesign::Revolution] Revolution001
  Angle = 360
  Axis = (0,-2e-16,1)
  Base = (0,0,0)
  Placement = pos=(0,0,0) rot=(1,0,0;1.5708rad)
  Profile = -> Sketch019
  ReferenceAxis = -> Sketch019 [V_Axis]
  Reversed = true
FEATURE [Sketcher::SketchObject] Sketch020
  MapMode = 5
  Placement = pos=(0,0,500) rot=(0,0,1;3.14159rad)
  Support = -> [Revolution001]
  sketch-geometry (8):
    g0: LineSegment StartX=-109.659 StartY=-60 StartZ=0 EndX=-109.659 EndY=60 EndZ=0
    g1: LineSegment StartX=-109.659 StartY=60 StartZ=0 EndX=-60 EndY=109.659 EndZ=0
    g2: LineSegment StartX=-60 StartY=109.659 StartZ=0 EndX=60 EndY=109.659 EndZ=0
    g3: LineSegment StartX=60 StartY=109.659 StartZ=0 EndX=109.659 EndY=60 EndZ=0
    g4: LineSegment StartX=109.659 StartY=60 StartZ=0 EndX=109.659 EndY=-60 EndZ=0
    g5: LineSegment StartX=109.659 StartY=-60 StartZ=0 EndX=60 EndY=-109.659 EndZ=0
    g6: LineSegment StartX=60 StartY=-109.659 StartZ=0 EndX=-60 EndY=-109.659 EndZ=0
    g7: LineSegment StartX=-60 StartY=-109.659 StartZ=0 EndX=-109.659 EndY=-60 EndZ=0
  constraints (21):
    c: Vertical(g0)
    c: Coincident(g0,g1)
    c: Coincident(g1,g2)
    c: Coincident(g2,g3)
    c: Coincident(g3,g4)
    c: Coincident(g4,g5)
    c: Coincident(g5,g6)
    c: Coincident(g6,g7)
    c: Coincident(g7,g0)
    c: Symmetric(g2,g1,g-2)
    c: Symmetric(g3,g4,g-1)
    c: Symmetric(g5,g6,g-2)
    c: DistanceY(g4,g4) = 120
    c: DistanceX(g6,g6) = 120
    c: DistanceY(g0,g0) = 120
    c: DistanceX(g2,g2) = 120
    c: Angle(g2,g3) = 2.35619
    c: Angle(g4,g5) = 2.35619
    c: Angle(g6,g7) = 2.35619
    c: Angle(g0,g1) = 2.35619
    c: Distance(g-1,g2) = 125
FEATURE [PartDesign::Pad] Pad012
  BaseFeature = -> Revolution001
  Direction = (1,1,1)
  Length = 20
  Length2 = 100
  Placement = pos=(0,0,0) rot=(1,0,0;1.5708rad)
  Profile = -> Sketch020
  Type = 0
FEATURE [PartDesign::Body] Body006
  Group = -> [Sketch019,Revolution001,Sketch020,Pad012]
  Origin = -> Origin016
  Tip = -> Pad012
PROVENANCE & LICENSES
A FreeCAD (.FCStd) document from a public repository crawl; recipes are the document's own serialized feature recipes (and, for linked parts, companion documents' recipes).
License: gpl-3.0.
